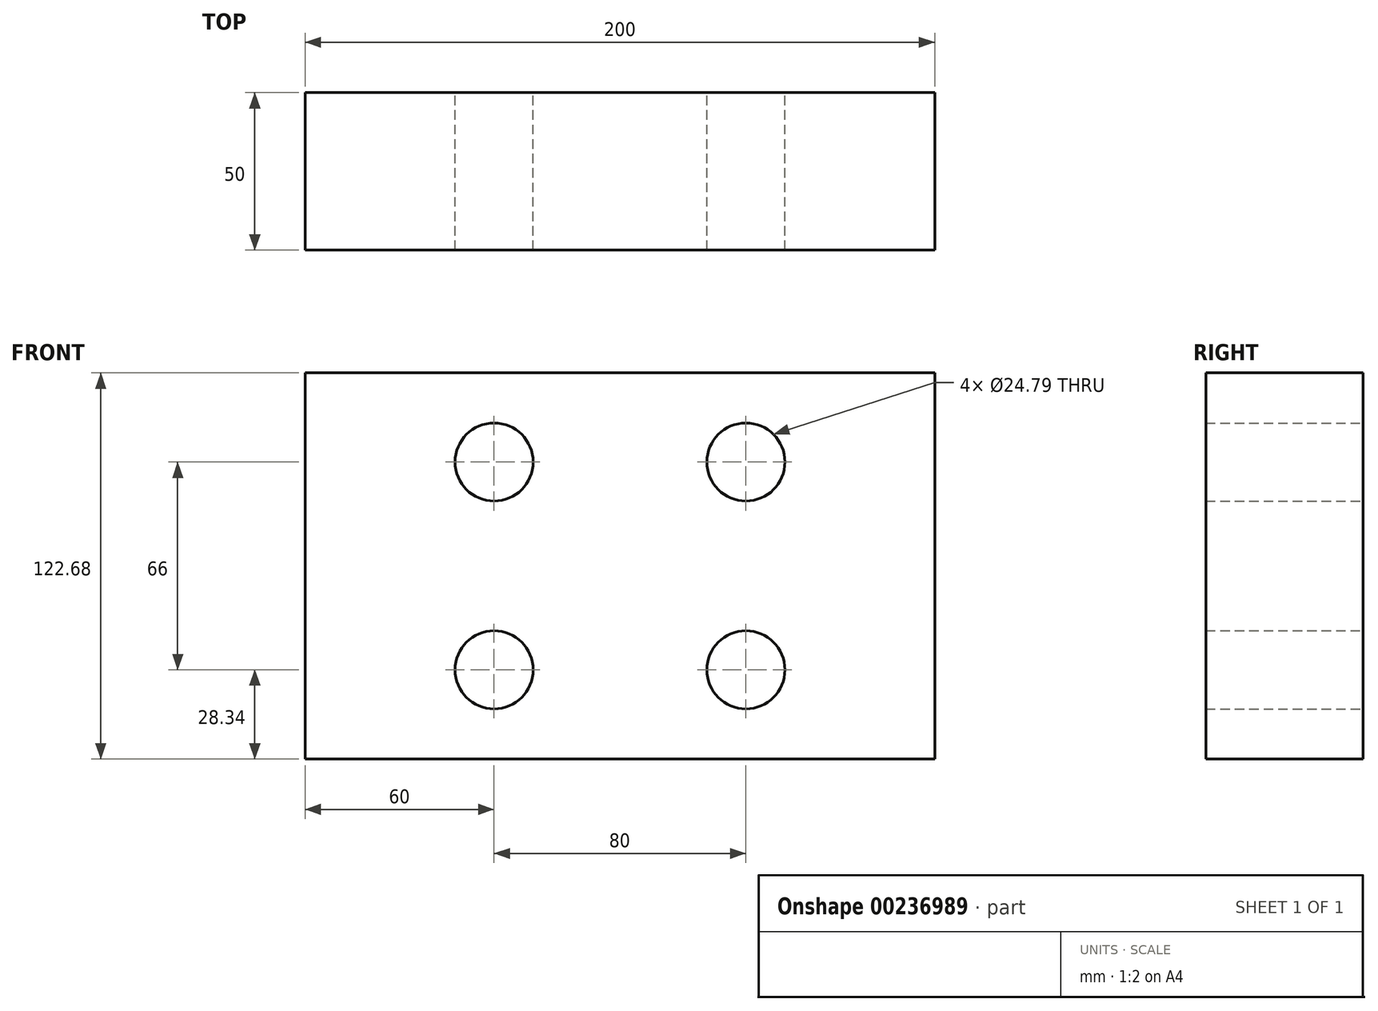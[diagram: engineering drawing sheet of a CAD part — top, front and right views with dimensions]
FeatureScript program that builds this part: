
annotation { "Feature Type Name" : "Feature", "Feature Type Description" : "" }
export const myFeature = defineFeature(function(context is Context, id is Id, definition is map)
    precondition{}
    {
        {
            var Q0;
            Q0=qCreatedBy(makeId("Front.planeOp"),FACE);
            var sketch = newSketch(context, id + "F0", { "sketchPlane" : qUnion([Q0])});
            skLineSegment(sketch, "E0.bottom", {"start": v(262.23, -140.5) * mm, "end": v(-262.23, -140.5) * mm});
            skLineSegment(sketch, "E0.top", {"start": v(262.23, 140.5) * mm, "end": v(-262.23, 140.5) * mm});
            skLineSegment(sketch, "E0.left", {"start": v(262.23, -140.5) * mm, "end": v(262.23, 140.5) * mm});
            skLineSegment(sketch, "E0.right", {"start": v(-262.23, -140.5) * mm, "end": v(-262.23, 140.5) * mm});
            skPoint(sketch, "E0.middle", {"position": v(0, 0) * mm});
            skLineSegment(sketch, "E1.bottom", {"start": v(100, 61.34) * mm, "end": v(-100, 61.34) * mm});
            skLineSegment(sketch, "E1.top", {"start": v(100, -61.34) * mm, "end": v(-100, -61.34) * mm});
            skLineSegment(sketch, "E1.left", {"start": v(100, -61.34) * mm, "end": v(100, 61.34) * mm});
            skLineSegment(sketch, "E1.right", {"start": v(-100, -61.34) * mm, "end": v(-100, 61.34) * mm});
            skCircle(sketch, "E2", {"center": v(40, 33) * mm, "radius": 12.4 * mm});
            skPoint(sketch, "E2.first.point", {"position": v(27.8, 30.8) * mm});
            skPoint(sketch, "E2.second.point", {"position": v(44.82, 21.58) * mm});
            skPoint(sketch, "E2.third.point", {"position": v(46.24, 22.3) * mm});
            skCircle(sketch, "E3.MirrorC", {"center": v(40, -33) * mm, "radius": 12.4 * mm});
            skPoint(sketch, "E4.MirrorP", {"position": v(46.24, -22.3) * mm});
            skPoint(sketch, "E5.MirrorP", {"position": v(44.82, -21.58) * mm});
            skPoint(sketch, "E6.MirrorP", {"position": v(27.8, -30.8) * mm});
            skCircle(sketch, "E7.MirrorC", {"center": v(-40, -33) * mm, "radius": 12.4 * mm});
            skCircle(sketch, "E8.MirrorC", {"center": v(-40, 33) * mm, "radius": 12.4 * mm});
            skPoint(sketch, "E9.MirrorP", {"position": v(-46.24, 22.3) * mm});
            skPoint(sketch, "E10.MirrorP", {"position": v(-27.8, -30.8) * mm});
            skPoint(sketch, "E11.MirrorP", {"position": v(-46.24, -22.3) * mm});
            skPoint(sketch, "E12.MirrorP", {"position": v(-27.8, 30.8) * mm});
            skPoint(sketch, "E13.MirrorP", {"position": v(-44.82, -21.58) * mm});
            skPoint(sketch, "E14.MirrorP", {"position": v(-44.82, 21.58) * mm});
            skSolve(sketch);
        }
        {
            var Q0;
            Q0=makeQuery(id+"F0.imprint","IMPRINT",FACE,{"disambiguationData":[TD([[makeQuery(id+"F0.imprint","IMPRINT",EDGE,{"derivedFrom":sQuery(id+"F0.wireOp",EDGE,"E1.bottom")}),1.0]])]});
            extrude(context, id + "F1", {"entities" : qUnion([Q0]), "depth" : 50 * mm});
        }
    });
